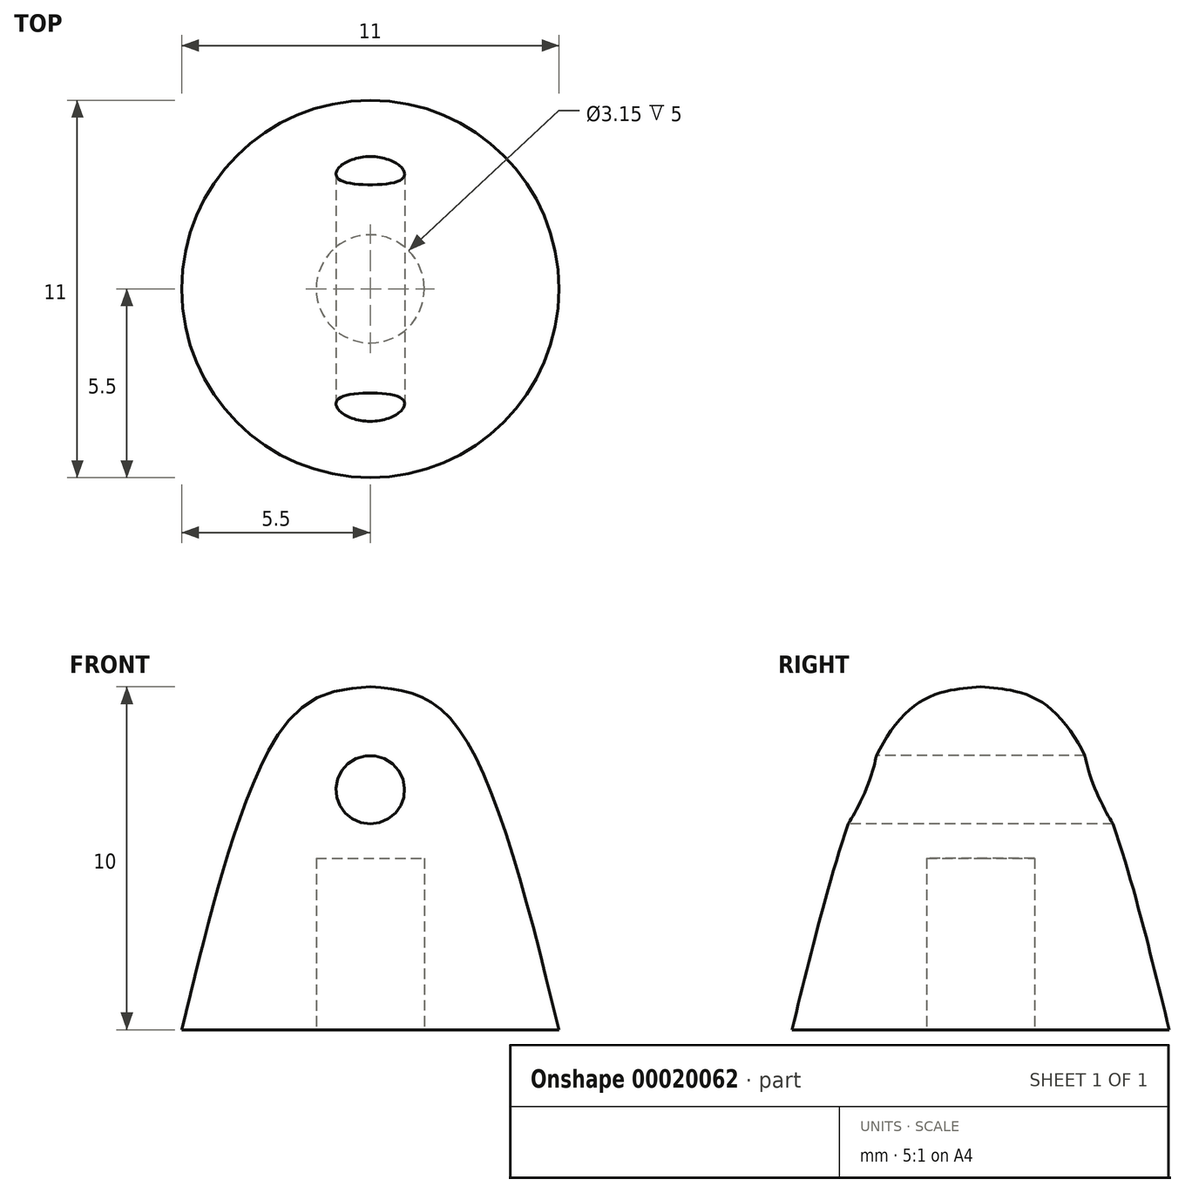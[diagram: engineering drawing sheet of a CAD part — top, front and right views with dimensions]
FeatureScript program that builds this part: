
annotation { "Feature Type Name" : "Feature", "Feature Type Description" : "" }
export const myFeature = defineFeature(function(context is Context, id is Id, definition is map)
    precondition{}
    {
        {
            var Q0;
            Q0=qCreatedBy(makeId("Front.planeOp"),FACE);
            var sketch = newSketch(context, id + "F0", { "sketchPlane" : qUnion([Q0])});
            skLineSegment(sketch, "E0.bottom", {"start": v(1.57, 0) * mm, "end": v(5.5, 0) * mm});
            skLineSegment(sketch, "E0.left", {"start": v(0, 5) * mm, "end": v(0, 10) * mm});
            skFitSpline(sketch, "E1", {"points": [v(0, 10) * mm, v(2.21, 9.2) * mm, v(5.5, 0) * mm], "startDerivative": vector(7.02, -0.55) * mm, "endDerivative": vector(4.3, -17.51) * mm});
            skLineSegment(sketch, "E2.top", {"start": v(0, 5) * mm, "end": v(1.57, 5) * mm});
            skLineSegment(sketch, "E2.right", {"start": v(1.57, 0) * mm, "end": v(1.57, 5) * mm});
            skSolve(sketch);
        }
        {
            var Q0;
            Q0=makeQuery(id+"F0.imprint","IMPRINT",FACE,{"disambiguationData":[TD([[makeQuery(id+"F0.imprint","IMPRINT",EDGE,{"derivedFrom":sQuery(id+"F0.wireOp",EDGE,"E0.bottom")}),1.0]])]});
            var Q1;
            Q1=sQuery(id+"F0.wireOp",EDGE,"E0.left");
            revolve(context, id + "F1", {"entities" : qUnion([Q0]), "axis" : qUnion([Q1]), "revolveType" : RevolveType.FULL});
        }
        {
            var Q0;
            Q0=qCreatedBy(makeId("Front.planeOp"),FACE);
            var sketch = newSketch(context, id + "F2", { "sketchPlane" : qUnion([Q0])});
            skCircle(sketch, "E3", {"center": v(0, 7) * mm, "radius": 1 * mm});
            skSolve(sketch);
        }
        {
            var Q0;
            Q0 = qSketchRegion(id + "F2", true);
            extrude(context, id + "F3", {"entities" : qUnion([Q0]), "operationType" : NewBodyOperationType.REMOVE, "endBound" : BoundingType.SYMMETRIC, "oppositeDirection" : true, "depth" : 10 * mm});
        }
    });
